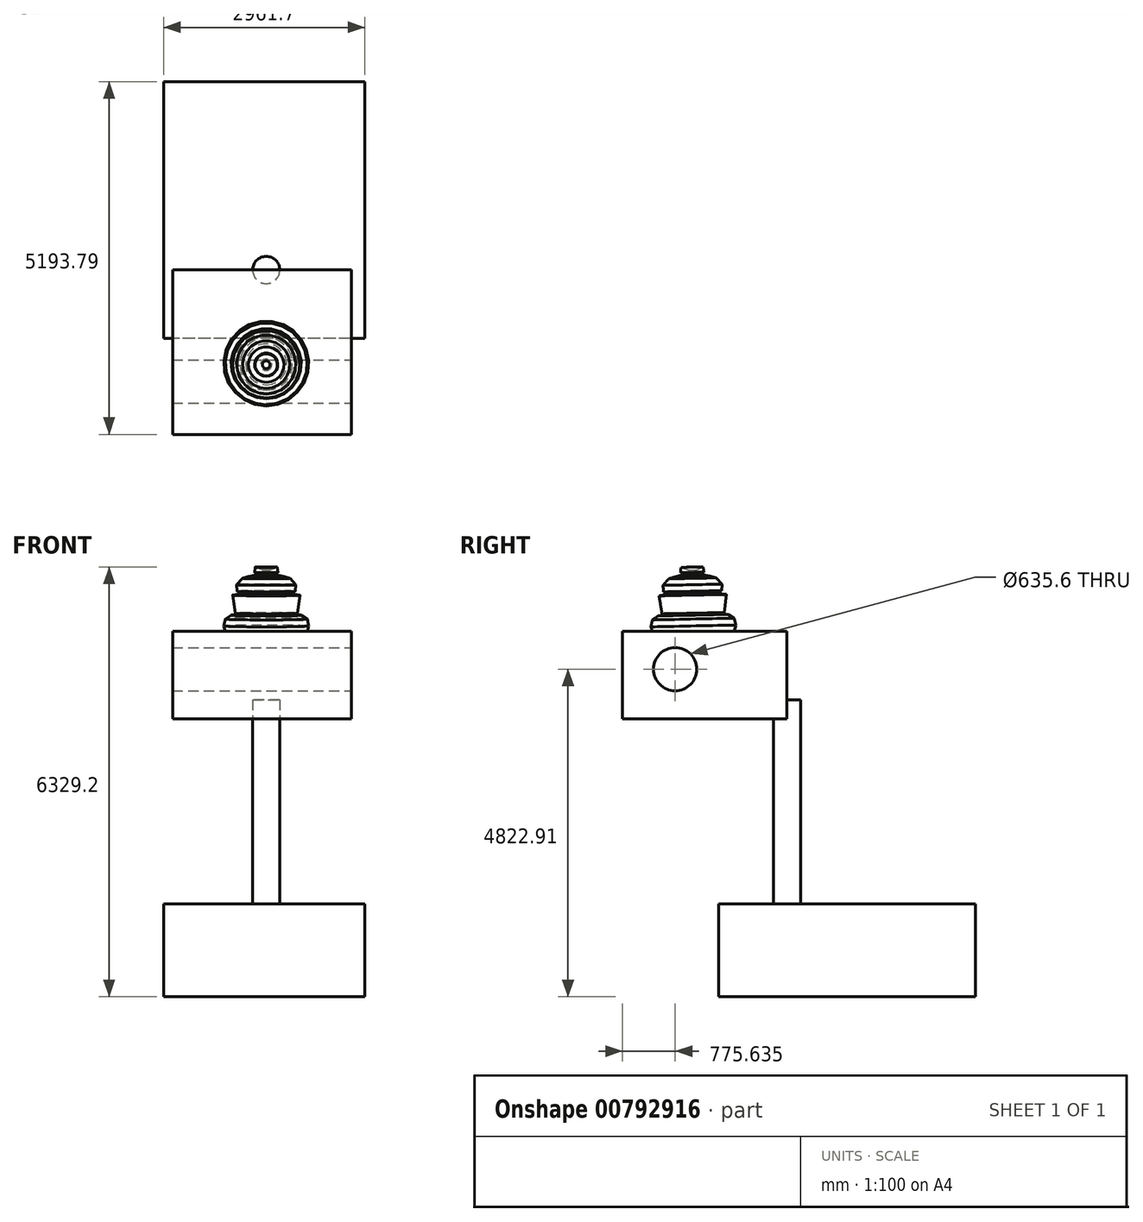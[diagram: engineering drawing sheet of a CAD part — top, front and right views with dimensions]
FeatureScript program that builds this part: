
annotation { "Feature Type Name" : "Feature", "Feature Type Description" : "" }
export const myFeature = defineFeature(function(context is Context, id is Id, definition is map)
    precondition{}
    {
        {
            var Q0;
            Q0=qCreatedBy(makeId("Top.planeOp"),FACE);
            var sketch = newSketch(context, id + "F0", { "sketchPlane" : qUnion([Q0])});
            skCircle(sketch, "E0", {"center": v(0, 0) * mm, "radius": 200 * mm});
            skSolve(sketch);
        }
        {
            var Q0;
            Q0 = qSketchRegion(id + "F0", true);
            extrude(context, id + "F1", {"entities" : qUnion([Q0]), "depth" : 3000 * mm, "offsetDistance" : 25 * mm});
        }
        {
            var Q0;
            Q0=qCreatedBy(makeId("Front.planeOp"),FACE);
            var sketch = newSketch(context, id + "F2", { "sketchPlane" : qUnion([Q0])});
            skLineSegment(sketch, "E1.bottom", {"start": v(-1376.28, 4012.51) * mm, "end": v(1254.78, 4012.51) * mm});
            skLineSegment(sketch, "E1.top", {"start": v(-1376.28, 2720.06) * mm, "end": v(1254.78, 2720.06) * mm});
            skLineSegment(sketch, "E1.left", {"start": v(-1376.28, 4012.51) * mm, "end": v(-1376.28, 2720.06) * mm});
            skLineSegment(sketch, "E1.right", {"start": v(1254.78, 4012.51) * mm, "end": v(1254.78, 2720.06) * mm});
            skSolve(sketch);
        }
        {
            var Q0;
            Q0 = qSketchRegion(id + "F2", true);
            extrude(context, id + "F3", {"entities" : qUnion([Q0]), "operationType" : NewBodyOperationType.ADD, "depth" : 2420 * mm, "offsetDistance" : 25 * mm});
        }
        {
            var Q0;
            Q0=qCreatedBy(makeId("Top.planeOp"),FACE);
            var sketch = newSketch(context, id + "F4", { "sketchPlane" : qUnion([Q0])});
            skLineSegment(sketch, "E2.bottom", {"start": v(1450.08, -1004.17) * mm, "end": v(-1511.62, -1004.17) * mm});
            skLineSegment(sketch, "E2.top", {"start": v(1450.08, 2773.8) * mm, "end": v(-1511.62, 2773.8) * mm});
            skLineSegment(sketch, "E2.left", {"start": v(1450.08, -1004.17) * mm, "end": v(1450.08, 2773.8) * mm});
            skLineSegment(sketch, "E2.right", {"start": v(-1511.62, -1004.17) * mm, "end": v(-1511.62, 2773.8) * mm});
            skSolve(sketch);
        }
        {
            var Q0;
            Q0 = qSketchRegion(id + "F4", true);
            extrude(context, id + "F5", {"entities" : qUnion([Q0]), "operationType" : NewBodyOperationType.ADD, "oppositeDirection" : true, "depth" : 1370 * mm, "offsetDistance" : 25 * mm});
        }
        {
            var Q0;
            Q0=makeQuery(id+"F3.opExtrude","SWEPT_FACE",FACE,{"disambiguationData":[OSD([sQuery(id+"F2.wireOp",EDGE,"E1.right")])]});
            var sketch = newSketch(context, id + "F6", { "sketchPlane" : qUnion([Q0])});
            skCircle(sketch, "E3", {"center": v(-1644.36, 3452.91) * mm, "radius": 317.8 * mm});
            skSolve(sketch);
        }
        {
            var Q0;
            Q0 = qSketchRegion(id + "F6", true);
            extrude(context, id + "F7", {"entities" : qUnion([Q0]), "operationType" : NewBodyOperationType.REMOVE, "oppositeDirection" : true, "depth" : 3360 * mm, "offsetDistance" : 25 * mm});
        }
        {
            var Q0;
            Q0=qCreatedBy(makeId("Right.planeOp"),FACE);
            var sketch = newSketch(context, id + "F8", { "sketchPlane" : qUnion([Q0])});
            skLineSegment(sketch, "E4", {"start": v(-1375.07, 3996.95) * mm, "end": v(-778.74, 3996.95) * mm});
            skLineSegment(sketch, "E5", {"start": v(-778.74, 3996.95) * mm, "end": v(-753.53, 4102.85) * mm});
            skLineSegment(sketch, "E6", {"start": v(-753.53, 4102.85) * mm, "end": v(-776.55, 4204.14) * mm});
            skLineSegment(sketch, "E7", {"start": v(-776.55, 4204.14) * mm, "end": v(-864.02, 4259.39) * mm});
            skLineSegment(sketch, "E8", {"start": v(-864.02, 4259.39) * mm, "end": v(-992.94, 4268.6) * mm});
            skLineSegment(sketch, "E9", {"start": v(-992.94, 4268.6) * mm, "end": v(-923.87, 4287) * mm});
            skLineSegment(sketch, "E10", {"start": v(-923.87, 4287) * mm, "end": v(-891.65, 4554.04) * mm});
            skLineSegment(sketch, "E11", {"start": v(-891.65, 4554.04) * mm, "end": v(-969.92, 4563.25) * mm});
            skLineSegment(sketch, "E12", {"start": v(-969.92, 4563.25) * mm, "end": v(-1085.02, 4586.27) * mm});
            skLineSegment(sketch, "E13", {"start": v(-1085.02, 4586.27) * mm, "end": v(-960.7, 4609.3) * mm});
            skLineSegment(sketch, "E14", {"start": v(-960.7, 4609.3) * mm, "end": v(-956.1, 4705.98) * mm});
            skLineSegment(sketch, "E15", {"start": v(-956.1, 4705.98) * mm, "end": v(-1043.58, 4798.06) * mm});
            skLineSegment(sketch, "E16", {"start": v(-1043.58, 4798.06) * mm, "end": v(-1131.06, 4821.08) * mm});
            skLineSegment(sketch, "E17", {"start": v(-1131.06, 4821.08) * mm, "end": v(-1310.61, 4857.91) * mm});
            skLineSegment(sketch, "E18", {"start": v(-1310.61, 4857.91) * mm, "end": v(-1223.14, 4880.93) * mm});
            skLineSegment(sketch, "E19", {"start": v(-1223.14, 4880.93) * mm, "end": v(-1232.35, 4959.2) * mm});
            skLineSegment(sketch, "E20", {"start": v(-1232.35, 4959.2) * mm, "end": v(-1338.24, 4913.16) * mm});
            skLineSegment(sketch, "E21", {"start": v(-1338.24, 4913.16) * mm, "end": v(-1393.49, 4848.7) * mm});
            skLineSegment(sketch, "E22", {"start": v(-1393.49, 4848.7) * mm, "end": v(-1375.07, 3996.95) * mm});
            skSolve(sketch);
        }
        {
            var Q0;
            Q0=makeQuery(id+"F8.imprint","IMPRINT",FACE,{"disambiguationData":[TD([[makeQuery(id+"F8.imprint","IMPRINT",EDGE,{"derivedFrom":sQuery(id+"F8.wireOp",EDGE,"E4")}),1.0]])]});
            var Q1;
            Q1=sQuery(id+"F8.wireOp",EDGE,"E22");
            revolve(context, id + "F9", {"operationType" : NewBodyOperationType.ADD, "surfaceOperationType" : NewSurfaceOperationType.NEW, "entities" : qUnion([Q0]), "axis" : qUnion([Q1]), "revolveType" : RevolveType.FULL});
        }
    });
